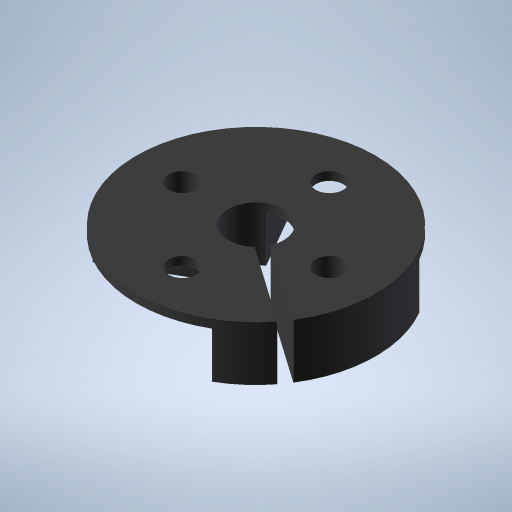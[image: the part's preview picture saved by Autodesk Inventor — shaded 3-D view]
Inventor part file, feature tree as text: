
AUTODESK INVENTOR PART (.ipt)
format: ipt  version: 2024 (Build 280153000, 153)  size: 313,344 bytes
history: native  units: in
note: dims shown in document units (in); Inventor stores cm internally (conversion verified against a paired STEP export)
features: other x4, extrude x4, hole x4, sketch x1
ambient origin geometry x8: Origin, YZ Plane, XZ Plane, XY Plane, X Axis, Y Axis, Z Axis, Center Point
bodies: Solid1 (feature_tree)
feature tree (13):
  other  "Annotations"
  sketch  "Sketch1"  dims[d0=0.3in d1=1.3in d2=0.4in d3=0.4in d4=0.12in d5=0.12in d6=0.296in d7=0.0in d8=0.396in d9=1.204in d10=0.4in d11=0.1875in d12=60.0deg d13=0.25in d14=0.0in d15=0.25in d16=0.0in d17=0.032in d18=0.032in d19=0.07in d24=0.12in d25=0.4in d26=0.12in d41=0.0625in d42=0.9963in d43=0.032in d44=0.032in d45=0.296in d46=0.0in d53=0.15in d54=0.5in d55=0.279in d56=0.25in d57=0.5635in d58=0.5in d59=0.0in d60=0.15in d61=0.75in d62=0.375in d63=0.25in d64=0.5635in d65=1.0in d66=0.0in d67=0.15in d68=0.75in d69=0.375in d70=0.25in d71=0.5635in d72=1.0in d73=0.0in d74=0.15in d75=0.75in d76=0.375in d77=0.25in d78=0.5635in d79=1.0in d80=0.0in d47=0.046in d48=2.2514in d49=0.65in d50=0.0in d51=0.3937in d52=0.296in]
  extrude  "Extrusion1"  Depth=0.296in
  extrude  "Extrusion2"  Depth=0.296in
  extrude  "Extrusion3"  Depth=0.296in
  extrude  "Extrusion6"  Depth=0.296in
  hole  "Hole3"  [1 undecoded]
  hole  "Hole4"  [1 undecoded]
  hole  "Hole5"  [1 undecoded]
  hole  "Hole6"  [1 undecoded]
  other  "Linear Dimension 1"
  other  "Radial Dimension 1"
  other  "Linear Dimension 2"
note: 4 required parameter values undecoded (feature->parameter linkage not recoverable at this tier; creation-order binding heuristic only, values carry confidence <= 0.55)
